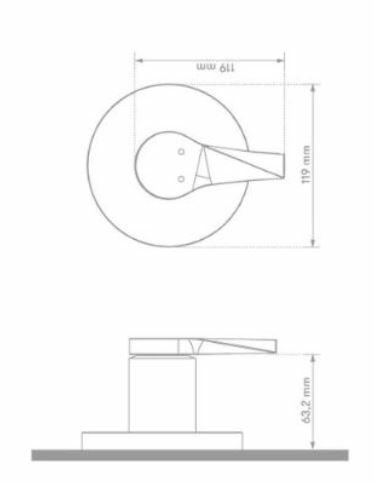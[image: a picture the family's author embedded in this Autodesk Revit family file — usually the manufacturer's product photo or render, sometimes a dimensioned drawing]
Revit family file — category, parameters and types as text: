
# Revit family: 01-0220-11SR-MEZCLADOR DUCHA 8 SIN SALIDA TINA COLECCIÓN PORTOBELLO
name_source: partatom
category: Aparatos sanitarios
revit_build: Autodesk Revit 2018 (Build: 20170223_1515(x64)
units: mm (PartAtom-declared; Revit-internal decimal feet)

## family parameters
Anfitrión = Cara
Compartido = No
Corte con vacíos al cargar = No
Cota de conector redondo = Diámetro de uso
Número OmniClass = 23.31.11.00
Punto de cálculo de habitación = No
Tipo de pieza = Normal

## types (1)
- 01-0220-11SR
    Alto = 57.5 mm
    Ancho = 70 mm
    Conexión AC = Sí
    Conexión AF = Sí
    Conexión de residuos = No
    Conexión de ventilación = No
    Descripción = Mezclador ducha
    Distancia entre griferias = 203.2 mm  [stored 0.666667 ft]
    Elevación por defecto = 0 mm  [stored 0 ft]
    Fabricante = Gricol
    Imagen de tipo = <Ninguno>
    Link Ficha Tecnica = https://infotecnica.gricol.com
    Metal Acero Inoxidable Cromado = Plastico ABS Cromado
    Metal Laton Cromado = Metal Laton Cromado
    Mezclador = Mezclador
    Modelo = 01-0220-11SR
    Plastico ABS Cromado = Plastico ABS Cromado
    Product Name = MEZCLADOR DUCHA SIN SALIDA TINA COLECCIÓN PORTOBELLO
    Profundidad = 72.5 mm  [stored 0.237861 ft]
    Sepacion entre registro y ducha = 400 mm  [stored 1.31234 ft]
    URL = https://www.gricol.com

note: [stored X ft] marks values corroborated as IEEE doubles in the binary element streams (Revit-internal decimal feet)

## geometry (parser evidence)
native form markers: Blend x2, Sweep x21
no freeform markers — native parametric forms only
